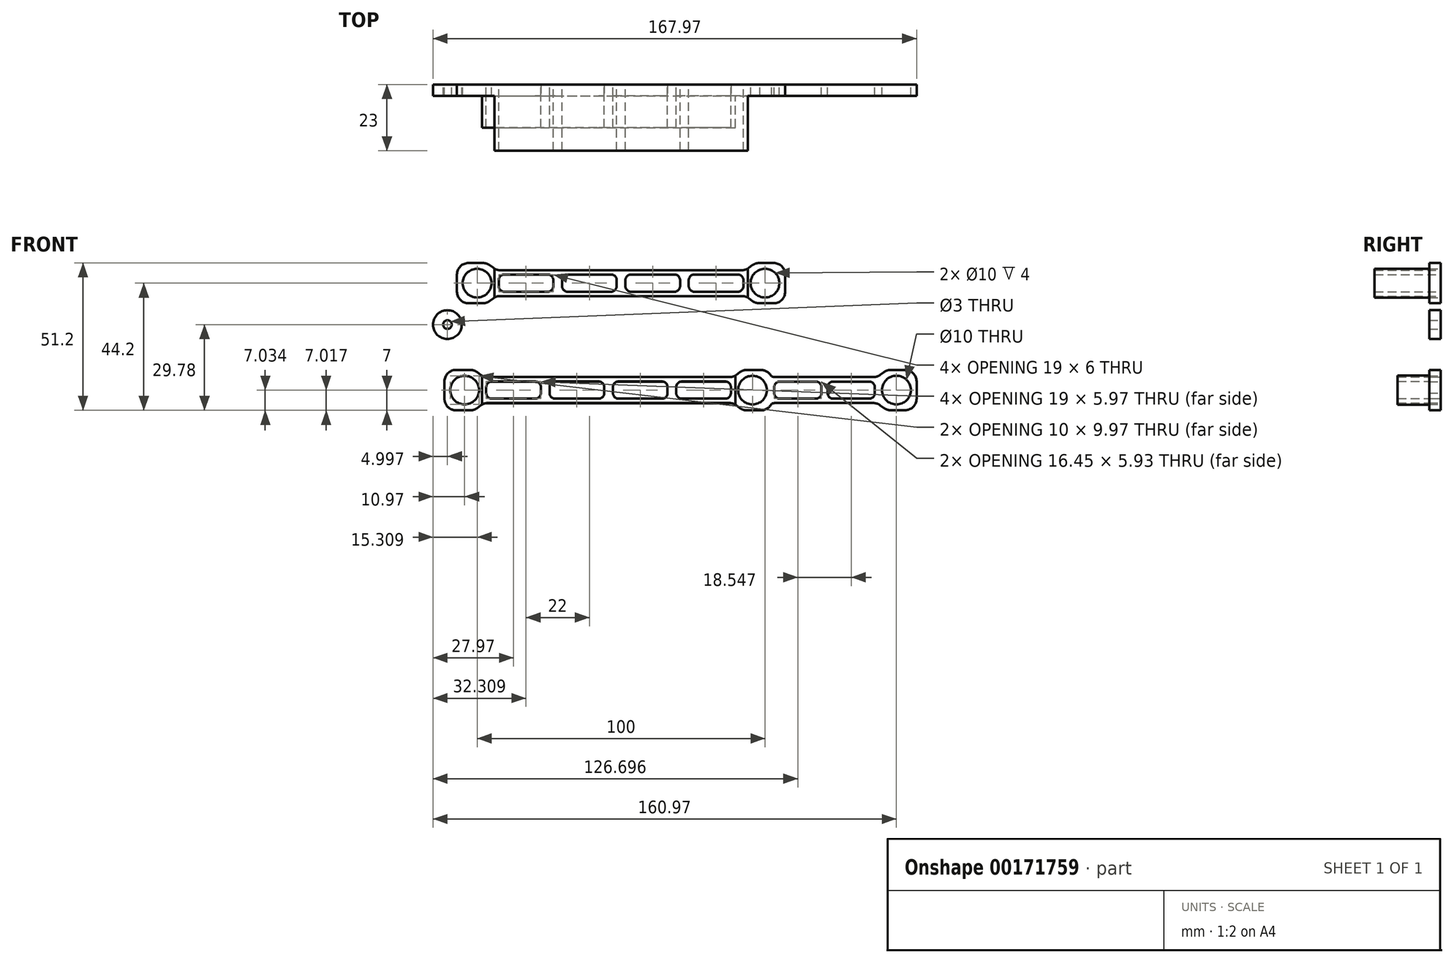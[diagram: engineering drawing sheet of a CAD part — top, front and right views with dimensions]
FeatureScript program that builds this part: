
annotation { "Feature Type Name" : "Feature", "Feature Type Description" : "" }
export const myFeature = defineFeature(function(context is Context, id is Id, definition is map)
    precondition{}
    {
        {
            var Q0;
            Q0=qCreatedBy(makeId("Front.planeOp"),FACE);
            var sketch = newSketch(context, id + "F0", { "sketchPlane" : qUnion([Q0])});
            skCircle(sketch, "E0", {"center": v(-50, 0) * mm, "radius": 5 * mm});
            skPoint(sketch, "E0.centerSnap0", {"position": v(-57, 0) * mm});
            skArc(sketch, "E1.filletArc", {"start": v(-57, -3) * mm, "mid": v(-55.83, -5.83) * mm, "end": v(-53, -7) * mm});
            skLineSegment(sketch, "E2.bottom", {"start": v(-40.5, -3) * mm, "end": v(-25.5, -3) * mm});
            skLineSegment(sketch, "E3.top", {"start": v(-18.5, -3) * mm, "end": v(-3.5, -3) * mm});
            skLineSegment(sketch, "E4", {"start": v(0, 16.94) * mm, "end": v(0, -22.86) * mm, "construction": true});
            skArc(sketch, "E5.filletArc", {"start": v(-25.5, -3) * mm, "mid": v(-24.09, -2.41) * mm, "end": v(-23.5, -1) * mm});
            skArc(sketch, "E6.filletArc", {"start": v(-42.5, -1) * mm, "mid": v(-41.91, -2.41) * mm, "end": v(-40.5, -3) * mm});
            skArc(sketch, "E7.filletArc", {"start": v(-20.5, -1) * mm, "mid": v(-19.91, -2.41) * mm, "end": v(-18.5, -3) * mm});
            skArc(sketch, "E8.filletArc", {"start": v(-3.5, -3) * mm, "mid": v(-2.09, -2.41) * mm, "end": v(-1.5, -1) * mm});
            skLineSegment(sketch, "E9", {"start": v(0, 0) * mm, "end": v(-64.75, 0) * mm, "construction": true});
            skLineSegment(sketch, "E10", {"start": v(-57, -3) * mm, "end": v(-57, 0) * mm});
            skLineSegment(sketch, "E11", {"start": v(-53, -7) * mm, "end": v(-48, -7) * mm});
            skLineSegment(sketch, "E12", {"start": v(-42, -4.5) * mm, "end": v(0, -4.5) * mm});
            skLineSegment(sketch, "E13", {"start": v(-42.5, -1) * mm, "end": v(-42.5, 0) * mm});
            skLineSegment(sketch, "E14", {"start": v(-23.5, -1) * mm, "end": v(-23.5, 0) * mm});
            skLineSegment(sketch, "E15", {"start": v(-20.5, -1) * mm, "end": v(-20.5, 0) * mm});
            skLineSegment(sketch, "E16", {"start": v(-1.5, -1) * mm, "end": v(-1.5, 0) * mm});
            skLineSegment(sketch, "E17", {"start": v(-45.6, -6.2) * mm, "end": v(-44.4, -5.3) * mm});
            skPoint(sketch, "E18.visualSharp", {"position": v(-46.67, -7) * mm});
            skArc(sketch, "E18.filletArc", {"start": v(-48, -7) * mm, "mid": v(-46.74, -6.8) * mm, "end": v(-45.6, -6.2) * mm});
            skPoint(sketch, "E19.visualSharp", {"position": v(-43.33, -4.5) * mm});
            skArc(sketch, "E19.filletArc", {"start": v(-42, -4.5) * mm, "mid": v(-43.26, -4.7) * mm, "end": v(-44.4, -5.3) * mm});
            skLineSegment(sketch, "E20.MirrorCS", {"start": v(-20.5, 1) * mm, "end": v(-20.5, 0) * mm});
            skLineSegment(sketch, "E21.MirrorCS", {"start": v(-23.5, 1) * mm, "end": v(-23.5, 0) * mm});
            skLineSegment(sketch, "E22.MirrorCS", {"start": v(-45.6, 6.2) * mm, "end": v(-44.4, 5.3) * mm});
            skLineSegment(sketch, "E23.MirrorCS", {"start": v(-42.5, 1) * mm, "end": v(-42.5, 0) * mm});
            skLineSegment(sketch, "E24.MirrorCS", {"start": v(-1.5, 1) * mm, "end": v(-1.5, 0) * mm});
            skArc(sketch, "E25.MirrorCS", {"start": v(-48, 7) * mm, "mid": v(-46.74, 6.8) * mm, "end": v(-45.6, 6.2) * mm});
            skArc(sketch, "E26.MirrorCS", {"start": v(-42, 4.5) * mm, "mid": v(-43.26, 4.7) * mm, "end": v(-44.4, 5.3) * mm});
            skLineSegment(sketch, "E27.MirrorCS", {"start": v(-40.5, 3) * mm, "end": v(-25.5, 3) * mm});
            skLineSegment(sketch, "E28.MirrorCS", {"start": v(-42, 4.5) * mm, "end": v(0, 4.5) * mm});
            skArc(sketch, "E29.MirrorCS", {"start": v(-57, 3) * mm, "mid": v(-55.83, 5.83) * mm, "end": v(-53, 7) * mm});
            skLineSegment(sketch, "E30.MirrorCS", {"start": v(-53, 7) * mm, "end": v(-48, 7) * mm});
            skLineSegment(sketch, "E31.MirrorCS", {"start": v(-57, 3) * mm, "end": v(-57, 0) * mm});
            skPoint(sketch, "E32.MirrorP", {"position": v(-46.67, 7) * mm});
            skLineSegment(sketch, "E33.MirrorCS", {"start": v(-18.5, 3) * mm, "end": v(-3.5, 3) * mm});
            skArc(sketch, "E34.MirrorCS", {"start": v(-3.5, 3) * mm, "mid": v(-2.09, 2.41) * mm, "end": v(-1.5, 1) * mm});
            skPoint(sketch, "E35.MirrorP", {"position": v(-43.33, 4.5) * mm});
            skArc(sketch, "E36.MirrorCS", {"start": v(-20.5, 1) * mm, "mid": v(-19.91, 2.41) * mm, "end": v(-18.5, 3) * mm});
            skArc(sketch, "E37.MirrorCS", {"start": v(-42.5, 1) * mm, "mid": v(-41.91, 2.41) * mm, "end": v(-40.5, 3) * mm});
            skArc(sketch, "E38.MirrorCS", {"start": v(-25.5, 3) * mm, "mid": v(-24.09, 2.41) * mm, "end": v(-23.5, 1) * mm});
            skLineSegment(sketch, "E39.MirrorCS", {"start": v(45.6, 6.2) * mm, "end": v(44.4, 5.3) * mm});
            skLineSegment(sketch, "E40.MirrorCS", {"start": v(23.5, 1) * mm, "end": v(23.5, 0) * mm});
            skLineSegment(sketch, "E41.MirrorCS", {"start": v(1.5, 1) * mm, "end": v(1.5, 0) * mm});
            skLineSegment(sketch, "E42.MirrorCS", {"start": v(42.5, -1) * mm, "end": v(42.5, 0) * mm});
            skLineSegment(sketch, "E43.MirrorCS", {"start": v(23.5, -1) * mm, "end": v(23.5, 0) * mm});
            skLineSegment(sketch, "E44.MirrorCS", {"start": v(20.5, -1) * mm, "end": v(20.5, 0) * mm});
            skLineSegment(sketch, "E45.MirrorCS", {"start": v(45.6, -6.2) * mm, "end": v(44.4, -5.3) * mm});
            skLineSegment(sketch, "E46.MirrorCS", {"start": v(20.5, 1) * mm, "end": v(20.5, 0) * mm});
            skLineSegment(sketch, "E47.MirrorCS", {"start": v(1.5, -1) * mm, "end": v(1.5, 0) * mm});
            skLineSegment(sketch, "E48.MirrorCS", {"start": v(42.5, 1) * mm, "end": v(42.5, 0) * mm});
            skArc(sketch, "E49.MirrorCS", {"start": v(48, 7) * mm, "mid": v(46.74, 6.8) * mm, "end": v(45.6, 6.2) * mm});
            skArc(sketch, "E50.MirrorCS", {"start": v(48, -7) * mm, "mid": v(46.74, -6.8) * mm, "end": v(45.6, -6.2) * mm});
            skArc(sketch, "E51.MirrorCS", {"start": v(42, -4.5) * mm, "mid": v(43.26, -4.7) * mm, "end": v(44.4, -5.3) * mm});
            skCircle(sketch, "E52.MirrorC", {"center": v(50, 0) * mm, "radius": 5 * mm});
            skPoint(sketch, "E53.MirrorP", {"position": v(57, 0) * mm});
            skArc(sketch, "E54.MirrorCS", {"start": v(42, 4.5) * mm, "mid": v(43.26, 4.7) * mm, "end": v(44.4, 5.3) * mm});
            skArc(sketch, "E55.MirrorCS", {"start": v(25.5, -3) * mm, "mid": v(24.09, -2.41) * mm, "end": v(23.5, -1) * mm});
            skLineSegment(sketch, "E56.MirrorCS", {"start": v(42, -4.5) * mm, "end": v(0, -4.5) * mm});
            skPoint(sketch, "E57.MirrorP", {"position": v(43.33, 4.5) * mm});
            skLineSegment(sketch, "E58.MirrorCS", {"start": v(18.5, -3) * mm, "end": v(3.5, -3) * mm});
            skArc(sketch, "E59.MirrorCS", {"start": v(57, -3) * mm, "mid": v(55.83, -5.83) * mm, "end": v(53, -7) * mm});
            skLineSegment(sketch, "E60.MirrorCS", {"start": v(53, -7) * mm, "end": v(48, -7) * mm});
            skArc(sketch, "E61.MirrorCS", {"start": v(25.5, 3) * mm, "mid": v(24.09, 2.41) * mm, "end": v(23.5, 1) * mm});
            skArc(sketch, "E62.MirrorCS", {"start": v(3.5, -3) * mm, "mid": v(2.09, -2.41) * mm, "end": v(1.5, -1) * mm});
            skArc(sketch, "E63.MirrorCS", {"start": v(57, 3) * mm, "mid": v(55.83, 5.83) * mm, "end": v(53, 7) * mm});
            skPoint(sketch, "E64.MirrorP", {"position": v(46.67, -7) * mm});
            skPoint(sketch, "E65.MirrorP", {"position": v(46.67, 7) * mm});
            skLineSegment(sketch, "E66.MirrorCS", {"start": v(53, 7) * mm, "end": v(48, 7) * mm});
            skPoint(sketch, "E67.MirrorP", {"position": v(43.33, -4.5) * mm});
            skArc(sketch, "E68.MirrorCS", {"start": v(42.5, 1) * mm, "mid": v(41.91, 2.41) * mm, "end": v(40.5, 3) * mm});
            skLineSegment(sketch, "E69.MirrorCS", {"start": v(42, 4.5) * mm, "end": v(0, 4.5) * mm});
            skArc(sketch, "E70.MirrorCS", {"start": v(20.5, 1) * mm, "mid": v(19.91, 2.41) * mm, "end": v(18.5, 3) * mm});
            skLineSegment(sketch, "E71.MirrorCS", {"start": v(0, 0) * mm, "end": v(64.75, 0) * mm, "construction": true});
            skArc(sketch, "E72.MirrorCS", {"start": v(3.5, 3) * mm, "mid": v(2.09, 2.41) * mm, "end": v(1.5, 1) * mm});
            skArc(sketch, "E73.MirrorCS", {"start": v(42.5, -1) * mm, "mid": v(41.91, -2.41) * mm, "end": v(40.5, -3) * mm});
            skArc(sketch, "E74.MirrorCS", {"start": v(20.5, -1) * mm, "mid": v(19.91, -2.41) * mm, "end": v(18.5, -3) * mm});
            skLineSegment(sketch, "E75.MirrorCS", {"start": v(57, 3) * mm, "end": v(57, 0) * mm});
            skLineSegment(sketch, "E76.MirrorCS", {"start": v(40.5, 3) * mm, "end": v(25.5, 3) * mm});
            skLineSegment(sketch, "E77.MirrorCS", {"start": v(40.5, -3) * mm, "end": v(25.5, -3) * mm});
            skLineSegment(sketch, "E78.MirrorCS", {"start": v(18.5, 3) * mm, "end": v(3.5, 3) * mm});
            skLineSegment(sketch, "E79.MirrorCS", {"start": v(57, -3) * mm, "end": v(57, 0) * mm});
            skSolve(sketch);
        }
        {
            var Q0;
            Q0=makeQuery(id+"F0.imprint","IMPRINT",FACE,{"disambiguationData":[TD([[makeQuery(id+"F0.imprint","IMPRINT",EDGE,{"derivedFrom":sQuery(id+"F0.wireOp",EDGE,"E1.filletArc")}),1.0]])]});
            extrude(context, id + "F1", {"entities" : qUnion([Q0]), "depth" : 4 * mm});
        }
        {
            var Q0;
            Q0=qCreatedBy(makeId("Front.planeOp"),FACE);
            var sketch = newSketch(context, id + "F2", { "sketchPlane" : qUnion([Q0])});
            skCircle(sketch, "E80", {"center": v(-55.97, 22.78) * mm, "radius": 1.5 * mm});
            skCircle(sketch, "E81", {"center": v(-55.97, 22.78) * mm, "radius": 5 * mm});
            skSolve(sketch);
        }
        {
            var Q0;
            Q0=makeQuery(id+"F2.imprint","IMPRINT",FACE,{"disambiguationData":[TD([[makeQuery(id+"F2.imprint","IMPRINT",EDGE,{"derivedFrom":sQuery(id+"F2.wireOp",EDGE,"E80")}),-1.0]])]});
            extrude(context, id + "F3", {"entities" : qUnion([Q0]), "depth" : 4 * mm});
        }
        {
            var Q0;
            Q0=qCreatedBy(makeId("Front.planeOp"),FACE);
            var sketch = newSketch(context, id + "F4", { "sketchPlane" : qUnion([Q0])});
            skCircle(sketch, "E82", {"center": v(-50, 0.03) * mm, "radius": 5 * mm});
            skPoint(sketch, "E82.centerSnap0", {"position": v(-57, 0.03) * mm});
            skArc(sketch, "E83.filletArc", {"start": v(-57, -2.97) * mm, "mid": v(-55.83, -5.8) * mm, "end": v(-53, -6.97) * mm});
            skLineSegment(sketch, "E84.bottom", {"start": v(-40.5, -2.97) * mm, "end": v(-25.5, -2.97) * mm});
            skLineSegment(sketch, "E85.top", {"start": v(-18.5, -2.97) * mm, "end": v(-3.5, -2.97) * mm});
            skLineSegment(sketch, "E86", {"start": v(0, 16.97) * mm, "end": v(0, -22.82) * mm, "construction": true});
            skArc(sketch, "E87.filletArc", {"start": v(-25.5, -2.97) * mm, "mid": v(-24.09, -2.38) * mm, "end": v(-23.5, -0.97) * mm});
            skArc(sketch, "E88.filletArc", {"start": v(-42.5, -0.97) * mm, "mid": v(-41.91, -2.38) * mm, "end": v(-40.5, -2.97) * mm});
            skArc(sketch, "E89.filletArc", {"start": v(-20.5, -0.97) * mm, "mid": v(-19.91, -2.38) * mm, "end": v(-18.5, -2.97) * mm});
            skArc(sketch, "E90.filletArc", {"start": v(-3.5, -2.97) * mm, "mid": v(-2.09, -2.38) * mm, "end": v(-1.5, -0.97) * mm});
            skLineSegment(sketch, "E91", {"start": v(0, 0.03) * mm, "end": v(-64.75, 0.03) * mm, "construction": true});
            skLineSegment(sketch, "E92", {"start": v(-57, -2.97) * mm, "end": v(-57, 0.03) * mm});
            skLineSegment(sketch, "E93", {"start": v(-53, -6.97) * mm, "end": v(-48, -6.97) * mm});
            skLineSegment(sketch, "E94", {"start": v(-42, -4.47) * mm, "end": v(0, -4.47) * mm});
            skLineSegment(sketch, "E95", {"start": v(-42.5, -0.97) * mm, "end": v(-42.5, 0.03) * mm});
            skLineSegment(sketch, "E96", {"start": v(-23.5, -0.97) * mm, "end": v(-23.5, 0.03) * mm});
            skLineSegment(sketch, "E97", {"start": v(-20.5, -0.97) * mm, "end": v(-20.5, 0.03) * mm});
            skLineSegment(sketch, "E98", {"start": v(-1.5, -0.97) * mm, "end": v(-1.5, 0.03) * mm});
            skLineSegment(sketch, "E99", {"start": v(-45.6, -6.17) * mm, "end": v(-44.4, -5.27) * mm});
            skPoint(sketch, "E100.visualSharp", {"position": v(-46.67, -6.97) * mm});
            skArc(sketch, "E100.filletArc", {"start": v(-48, -6.97) * mm, "mid": v(-46.74, -6.76) * mm, "end": v(-45.6, -6.17) * mm});
            skPoint(sketch, "E101.visualSharp", {"position": v(-43.33, -4.47) * mm});
            skArc(sketch, "E101.filletArc", {"start": v(-42, -4.47) * mm, "mid": v(-43.26, -4.67) * mm, "end": v(-44.4, -5.27) * mm});
            skLineSegment(sketch, "E102.MirrorCS", {"start": v(-20.5, 1.03) * mm, "end": v(-20.5, 0.03) * mm});
            skLineSegment(sketch, "E103.MirrorCS", {"start": v(-23.5, 1.03) * mm, "end": v(-23.5, 0.03) * mm});
            skLineSegment(sketch, "E104.MirrorCS", {"start": v(-45.6, 6.23) * mm, "end": v(-44.4, 5.33) * mm});
            skLineSegment(sketch, "E105.MirrorCS", {"start": v(-42.5, 1.03) * mm, "end": v(-42.5, 0.03) * mm});
            skLineSegment(sketch, "E106.MirrorCS", {"start": v(-1.5, 1.03) * mm, "end": v(-1.5, 0.03) * mm});
            skArc(sketch, "E107.MirrorCS", {"start": v(-48, 7.03) * mm, "mid": v(-46.74, 6.83) * mm, "end": v(-45.6, 6.23) * mm});
            skArc(sketch, "E108.MirrorCS", {"start": v(-42, 4.53) * mm, "mid": v(-43.26, 4.74) * mm, "end": v(-44.4, 5.33) * mm});
            skLineSegment(sketch, "E109.MirrorCS", {"start": v(-40.5, 3.03) * mm, "end": v(-25.5, 3.03) * mm});
            skLineSegment(sketch, "E110.MirrorCS", {"start": v(-42, 4.53) * mm, "end": v(0, 4.53) * mm});
            skArc(sketch, "E111.MirrorCS", {"start": v(-57, 3.03) * mm, "mid": v(-55.83, 5.86) * mm, "end": v(-53, 7.03) * mm});
            skLineSegment(sketch, "E112.MirrorCS", {"start": v(-53, 7.03) * mm, "end": v(-48, 7.03) * mm});
            skLineSegment(sketch, "E113.MirrorCS", {"start": v(-57, 3.03) * mm, "end": v(-57, 0.03) * mm});
            skPoint(sketch, "E114.MirrorP", {"position": v(-46.67, 7.03) * mm});
            skLineSegment(sketch, "E115.MirrorCS", {"start": v(-18.5, 3.03) * mm, "end": v(-3.5, 3.03) * mm});
            skArc(sketch, "E116.MirrorCS", {"start": v(-3.5, 3.03) * mm, "mid": v(-2.09, 2.45) * mm, "end": v(-1.5, 1.03) * mm});
            skPoint(sketch, "E117.MirrorP", {"position": v(-43.33, 4.53) * mm});
            skArc(sketch, "E118.MirrorCS", {"start": v(-20.5, 1.03) * mm, "mid": v(-19.91, 2.45) * mm, "end": v(-18.5, 3.03) * mm});
            skArc(sketch, "E119.MirrorCS", {"start": v(-42.5, 1.03) * mm, "mid": v(-41.91, 2.45) * mm, "end": v(-40.5, 3.03) * mm});
            skArc(sketch, "E120.MirrorCS", {"start": v(-25.5, 3.03) * mm, "mid": v(-24.09, 2.45) * mm, "end": v(-23.5, 1.03) * mm});
            skLineSegment(sketch, "E121.MirrorCS", {"start": v(45.6, 6.23) * mm, "end": v(44.4, 5.33) * mm});
            skLineSegment(sketch, "E122.MirrorCS", {"start": v(23.5, 1.03) * mm, "end": v(23.5, 0.03) * mm});
            skLineSegment(sketch, "E123.MirrorCS", {"start": v(1.5, 1.03) * mm, "end": v(1.5, 0.03) * mm});
            skLineSegment(sketch, "E124.MirrorCS", {"start": v(42.5, -0.97) * mm, "end": v(42.5, 0.03) * mm});
            skLineSegment(sketch, "E125.MirrorCS", {"start": v(23.5, -0.97) * mm, "end": v(23.5, 0.03) * mm});
            skLineSegment(sketch, "E126.MirrorCS", {"start": v(20.5, -0.97) * mm, "end": v(20.5, 0.03) * mm});
            skLineSegment(sketch, "E127.MirrorCS", {"start": v(45.6, -6.17) * mm, "end": v(44.4, -5.27) * mm});
            skLineSegment(sketch, "E128.MirrorCS", {"start": v(20.5, 1.03) * mm, "end": v(20.5, 0.03) * mm});
            skLineSegment(sketch, "E129.MirrorCS", {"start": v(1.5, -0.97) * mm, "end": v(1.5, 0.03) * mm});
            skLineSegment(sketch, "E130.MirrorCS", {"start": v(42.5, 1.03) * mm, "end": v(42.5, 0.03) * mm});
            skArc(sketch, "E131.MirrorCS", {"start": v(48, 7.03) * mm, "mid": v(46.74, 6.83) * mm, "end": v(45.6, 6.23) * mm});
            skArc(sketch, "E132.MirrorCS", {"start": v(48, -6.97) * mm, "mid": v(46.74, -6.76) * mm, "end": v(45.6, -6.17) * mm});
            skArc(sketch, "E133.MirrorCS", {"start": v(42, -4.47) * mm, "mid": v(43.26, -4.67) * mm, "end": v(44.4, -5.27) * mm});
            skCircle(sketch, "E134.MirrorC", {"center": v(50, 0.03) * mm, "radius": 5 * mm});
            skArc(sketch, "E135.MirrorCS", {"start": v(42, 4.53) * mm, "mid": v(43.26, 4.74) * mm, "end": v(44.4, 5.33) * mm});
            skArc(sketch, "E136.MirrorCS", {"start": v(25.5, -2.97) * mm, "mid": v(24.09, -2.38) * mm, "end": v(23.5, -0.97) * mm});
            skLineSegment(sketch, "E137.MirrorCS", {"start": v(42, -4.47) * mm, "end": v(0, -4.47) * mm});
            skPoint(sketch, "E138.MirrorP", {"position": v(43.33, 4.53) * mm});
            skLineSegment(sketch, "E139.MirrorCS", {"start": v(18.5, -2.97) * mm, "end": v(3.5, -2.97) * mm});
            skArc(sketch, "E140.MirrorCS", {"start": v(25.5, 3.03) * mm, "mid": v(24.09, 2.45) * mm, "end": v(23.5, 1.03) * mm});
            skArc(sketch, "E141.MirrorCS", {"start": v(3.5, -2.97) * mm, "mid": v(2.09, -2.38) * mm, "end": v(1.5, -0.97) * mm});
            skPoint(sketch, "E142.MirrorP", {"position": v(46.67, -6.97) * mm});
            skPoint(sketch, "E143.MirrorP", {"position": v(46.67, 7.03) * mm});
            skPoint(sketch, "E144.MirrorP", {"position": v(43.33, -4.47) * mm});
            skArc(sketch, "E145.MirrorCS", {"start": v(42.5, 1.03) * mm, "mid": v(41.91, 2.45) * mm, "end": v(40.5, 3.03) * mm});
            skLineSegment(sketch, "E146.MirrorCS", {"start": v(42, 4.53) * mm, "end": v(0, 4.53) * mm});
            skArc(sketch, "E147.MirrorCS", {"start": v(20.5, 1.03) * mm, "mid": v(19.91, 2.45) * mm, "end": v(18.5, 3.03) * mm});
            skLineSegment(sketch, "E148.MirrorCS", {"start": v(0, 0.03) * mm, "end": v(64.75, 0.03) * mm, "construction": true});
            skArc(sketch, "E149.MirrorCS", {"start": v(3.5, 3.03) * mm, "mid": v(2.09, 2.45) * mm, "end": v(1.5, 1.03) * mm});
            skArc(sketch, "E150.MirrorCS", {"start": v(42.5, -0.97) * mm, "mid": v(41.91, -2.38) * mm, "end": v(40.5, -2.97) * mm});
            skArc(sketch, "E151.MirrorCS", {"start": v(20.5, -0.97) * mm, "mid": v(19.91, -2.38) * mm, "end": v(18.5, -2.97) * mm});
            skLineSegment(sketch, "E152.MirrorCS", {"start": v(40.5, 3.03) * mm, "end": v(25.5, 3.03) * mm});
            skLineSegment(sketch, "E153.MirrorCS", {"start": v(40.5, -2.97) * mm, "end": v(25.5, -2.97) * mm});
            skLineSegment(sketch, "E154.MirrorCS", {"start": v(18.5, 3.03) * mm, "end": v(3.5, 3.03) * mm});
            skLineSegment(sketch, "E155", {"start": v(25, -18.9) * mm, "end": v(25, 17.57) * mm, "construction": true});
            skLineSegment(sketch, "E156.MirrorCS", {"start": v(95.6, 6.23) * mm, "end": v(94.4, 5.33) * mm});
            skLineSegment(sketch, "E157.MirrorCS", {"start": v(95.6, -6.17) * mm, "end": v(94.4, -5.27) * mm});
            skCircle(sketch, "E158.MirrorC", {"center": v(100, 0.03) * mm, "radius": 5 * mm});
            skPoint(sketch, "E159.MirrorP", {"position": v(107, 0.03) * mm});
            skArc(sketch, "E160.MirrorCS", {"start": v(98, 7.03) * mm, "mid": v(96.74, 6.83) * mm, "end": v(95.6, 6.23) * mm});
            skArc(sketch, "E161.MirrorCS", {"start": v(98, -6.97) * mm, "mid": v(96.74, -6.76) * mm, "end": v(95.6, -6.17) * mm});
            skLineSegment(sketch, "E162.MirrorCS", {"start": v(107, 3.03) * mm, "end": v(107, 0.03) * mm});
            skPoint(sketch, "E163.MirrorP", {"position": v(96.67, -6.97) * mm});
            skLineSegment(sketch, "E164.MirrorCS", {"start": v(103, 7.03) * mm, "end": v(98, 7.03) * mm});
            skLineSegment(sketch, "E165.MirrorCS", {"start": v(103, -6.97) * mm, "end": v(98, -6.97) * mm});
            skLineSegment(sketch, "E166.MirrorCS", {"start": v(107, -2.97) * mm, "end": v(107, 0.03) * mm});
            skArc(sketch, "E167.MirrorCS", {"start": v(107, -2.97) * mm, "mid": v(105.83, -5.8) * mm, "end": v(103, -6.97) * mm});
            skArc(sketch, "E168.MirrorCS", {"start": v(107, 3.03) * mm, "mid": v(105.83, 5.86) * mm, "end": v(103, 7.03) * mm});
            skPoint(sketch, "E169.MirrorP", {"position": v(96.67, 7.03) * mm});
            skPoint(sketch, "E170.MirrorP", {"position": v(93.33, -4.47) * mm});
            skPoint(sketch, "E171.MirrorP", {"position": v(93.33, 4.53) * mm});
            skArc(sketch, "E172.MirrorCS", {"start": v(92, 4.53) * mm, "mid": v(93.26, 4.74) * mm, "end": v(94.4, 5.33) * mm});
            skArc(sketch, "E173.MirrorCS", {"start": v(92, -4.47) * mm, "mid": v(93.26, -4.67) * mm, "end": v(94.4, -5.27) * mm});
            skLineSegment(sketch, "E174", {"start": v(50, -9.2) * mm, "end": v(50, 12.58) * mm, "construction": true});
            skLineSegment(sketch, "E175", {"start": v(48, 7.03) * mm, "end": v(50, 7.03) * mm});
            skLineSegment(sketch, "E176", {"start": v(48, -6.97) * mm, "end": v(50, -6.97) * mm});
            skLineSegment(sketch, "E177.MirrorCS", {"start": v(52, 7.03) * mm, "end": v(50, 7.03) * mm});
            skArc(sketch, "E178.MirrorCS", {"start": v(52, 7.03) * mm, "mid": v(53.26, 6.83) * mm, "end": v(54.4, 6.23) * mm});
            skLineSegment(sketch, "E179.MirrorCS", {"start": v(54.4, 6.23) * mm, "end": v(55.6, 5.33) * mm});
            skArc(sketch, "E180.MirrorCS", {"start": v(58, 4.53) * mm, "mid": v(56.74, 4.74) * mm, "end": v(55.6, 5.33) * mm});
            skArc(sketch, "E181.MirrorCS", {"start": v(58, -4.47) * mm, "mid": v(56.74, -4.67) * mm, "end": v(55.6, -5.27) * mm});
            skLineSegment(sketch, "E182.MirrorCS", {"start": v(54.4, -6.17) * mm, "end": v(55.6, -5.27) * mm});
            skArc(sketch, "E183.MirrorCS", {"start": v(52, -6.97) * mm, "mid": v(53.26, -6.76) * mm, "end": v(54.4, -6.17) * mm});
            skLineSegment(sketch, "E184.MirrorCS", {"start": v(52, -6.97) * mm, "end": v(50, -6.97) * mm});
            skLineSegment(sketch, "E185", {"start": v(58, 4.53) * mm, "end": v(92, 4.53) * mm});
            skLineSegment(sketch, "E186", {"start": v(58, -4.47) * mm, "end": v(92, -4.47) * mm});
            skLineSegment(sketch, "E187.bottom", {"start": v(71.95, -2.97) * mm, "end": v(59.5, -2.97) * mm});
            skLineSegment(sketch, "E187.top", {"start": v(71.95, 2.97) * mm, "end": v(59.5, 2.97) * mm});
            skLineSegment(sketch, "E187.left", {"start": v(73.95, -0.97) * mm, "end": v(73.95, 0.97) * mm});
            skLineSegment(sketch, "E187.right", {"start": v(57.5, -0.97) * mm, "end": v(57.5, 0.97) * mm});
            skPoint(sketch, "E187.middle", {"position": v(65.73, 0) * mm});
            skPoint(sketch, "E188.visualSharp", {"position": v(57.5, 2.97) * mm});
            skArc(sketch, "E188.filletArc", {"start": v(59.5, 2.97) * mm, "mid": v(58.09, 2.38) * mm, "end": v(57.5, 0.97) * mm});
            skPoint(sketch, "E189.visualSharp", {"position": v(57.5, -2.97) * mm});
            skArc(sketch, "E189.filletArc", {"start": v(57.5, -0.97) * mm, "mid": v(58.09, -2.38) * mm, "end": v(59.5, -2.97) * mm});
            skPoint(sketch, "E190.visualSharp", {"position": v(73.95, -2.97) * mm});
            skArc(sketch, "E190.filletArc", {"start": v(71.95, -2.97) * mm, "mid": v(73.37, -2.38) * mm, "end": v(73.95, -0.97) * mm});
            skPoint(sketch, "E191.visualSharp", {"position": v(73.95, 2.97) * mm});
            skArc(sketch, "E191.filletArc", {"start": v(73.95, 0.97) * mm, "mid": v(73.37, 2.38) * mm, "end": v(71.95, 2.97) * mm});
            skLineSegment(sketch, "E192", {"start": v(75, -8.26) * mm, "end": v(75, 11.45) * mm, "construction": true});
            skPoint(sketch, "E192.startSnap0", {"position": v(75, -4.47) * mm});
            skArc(sketch, "E193.MirrorCS", {"start": v(90.5, 2.97) * mm, "mid": v(91.91, 2.38) * mm, "end": v(92.5, 0.97) * mm});
            skLineSegment(sketch, "E194.MirrorCS", {"start": v(150, 0.03) * mm, "end": v(85.25, 0.03) * mm, "construction": true});
            skLineSegment(sketch, "E195.MirrorCS", {"start": v(92.5, -0.97) * mm, "end": v(92.5, 0.97) * mm});
            skPoint(sketch, "E196.MirrorP", {"position": v(76.05, 2.97) * mm});
            skArc(sketch, "E197.MirrorCS", {"start": v(76.05, 0.97) * mm, "mid": v(76.63, 2.38) * mm, "end": v(78.05, 2.97) * mm});
            skArc(sketch, "E198.MirrorCS", {"start": v(78.05, -2.97) * mm, "mid": v(76.63, -2.38) * mm, "end": v(76.05, -0.97) * mm});
            skPoint(sketch, "E199.MirrorP", {"position": v(76.05, -2.97) * mm});
            skPoint(sketch, "E200.MirrorP", {"position": v(92.5, -2.97) * mm});
            skLineSegment(sketch, "E201.MirrorCS", {"start": v(76.05, -0.97) * mm, "end": v(76.05, 0.97) * mm});
            skPoint(sketch, "E202.MirrorP", {"position": v(92.5, 2.97) * mm});
            skPoint(sketch, "E203.MirrorP", {"position": v(84.27, 0) * mm});
            skLineSegment(sketch, "E204.MirrorCS", {"start": v(78.05, 2.97) * mm, "end": v(90.5, 2.97) * mm});
            skLineSegment(sketch, "E205.MirrorCS", {"start": v(78.05, -2.97) * mm, "end": v(90.5, -2.97) * mm});
            skArc(sketch, "E206.MirrorCS", {"start": v(92.5, -0.97) * mm, "mid": v(91.91, -2.38) * mm, "end": v(90.5, -2.97) * mm});
            skLineSegment(sketch, "E207", {"start": v(-44, 5.07) * mm, "end": v(-44, -5) * mm});
            skLineSegment(sketch, "E208", {"start": v(44, 5.07) * mm, "end": v(44, -5) * mm});
            skSolve(sketch);
        }
        {
            var Q0;
            Q0=makeQuery(id+"F4.imprint","IMPRINT",FACE,{"disambiguationData":[TD([[makeQuery(id+"F4.imprint","IMPRINT",EDGE,{"derivedFrom":sQuery(id+"F4.wireOp",EDGE,"E83.filletArc")}),1.0]])]});
            var Q1;
            {var subQ5=sQuery(id+"F4.wireOp",EDGE,"E84.bottom");Q1=makeQuery(id+"F4.imprint","IMPRINT",FACE,{"disambiguationData":[TD([[makeQuery(id+"F4.imprint","IMPRINT",EDGE,{"derivedFrom":subQ5}),-1.0]])]});}
            var Q2;
            Q2=makeQuery(id+"F4.imprint","IMPRINT",FACE,{"disambiguationData":[TD([[makeQuery(id+"F4.imprint","IMPRINT",EDGE,{"derivedFrom":sQuery(id+"F4.wireOp",EDGE,"E121.MirrorCS")}),1.0]])]});
            extrude(context, id + "F5", {"entities" : qUnion([Q0, Q1, Q2]), "depth" : 4 * mm});
        }
        {
            var Q0;
            {var subQ5=sQuery(id+"F4.wireOp",EDGE,"E84.bottom");Q0=makeQuery(id+"F4.imprint","IMPRINT",FACE,{"disambiguationData":[TD([[makeQuery(id+"F4.imprint","IMPRINT",EDGE,{"derivedFrom":subQ5}),-1.0]])]});}
            extrude(context, id + "F6", {"entities" : qUnion([Q0]), "operationType" : NewBodyOperationType.ADD, "depth" : 15 * mm});
        }
        {
            var Q0;
            Q0=qCreatedBy(makeId("Front.planeOp"),FACE);
            var sketch = newSketch(context, id + "F7", { "sketchPlane" : qUnion([Q0])});
            skCircle(sketch, "E209", {"center": v(-45.66, 37.2) * mm, "radius": 5 * mm});
            skPoint(sketch, "E209.centerSnap0", {"position": v(-52.66, 37.2) * mm});
            skArc(sketch, "E210.filletArc", {"start": v(-52.66, 34.2) * mm, "mid": v(-51.49, 31.37) * mm, "end": v(-48.66, 30.2) * mm});
            skLineSegment(sketch, "E211.bottom", {"start": v(-36.16, 34.2) * mm, "end": v(-21.16, 34.2) * mm});
            skLineSegment(sketch, "E212.top", {"start": v(-14.16, 34.2) * mm, "end": v(0.84, 34.2) * mm});
            skLineSegment(sketch, "E213", {"start": v(4.34, 51.7) * mm, "end": v(4.34, 22.7) * mm, "construction": true});
            skArc(sketch, "E214.filletArc", {"start": v(-21.16, 34.2) * mm, "mid": v(-19.75, 34.79) * mm, "end": v(-19.16, 36.2) * mm});
            skArc(sketch, "E215.filletArc", {"start": v(-38.16, 36.2) * mm, "mid": v(-37.57, 34.79) * mm, "end": v(-36.16, 34.2) * mm});
            skArc(sketch, "E216.filletArc", {"start": v(-16.16, 36.2) * mm, "mid": v(-15.57, 34.79) * mm, "end": v(-14.16, 34.2) * mm});
            skArc(sketch, "E217.filletArc", {"start": v(0.84, 34.2) * mm, "mid": v(2.25, 34.79) * mm, "end": v(2.84, 36.2) * mm});
            skLineSegment(sketch, "E218", {"start": v(4.34, 37.2) * mm, "end": v(-62.66, 37.2) * mm, "construction": true});
            skLineSegment(sketch, "E219", {"start": v(-52.66, 34.2) * mm, "end": v(-52.66, 37.2) * mm});
            skLineSegment(sketch, "E220", {"start": v(-48.66, 30.2) * mm, "end": v(-43.66, 30.2) * mm});
            skLineSegment(sketch, "E221", {"start": v(-37.66, 32.7) * mm, "end": v(4.34, 32.7) * mm});
            skLineSegment(sketch, "E222", {"start": v(-38.16, 36.2) * mm, "end": v(-38.16, 37.2) * mm});
            skLineSegment(sketch, "E223", {"start": v(-19.16, 36.2) * mm, "end": v(-19.16, 37.2) * mm});
            skLineSegment(sketch, "E224", {"start": v(-16.16, 36.2) * mm, "end": v(-16.16, 37.2) * mm});
            skLineSegment(sketch, "E225", {"start": v(2.84, 36.2) * mm, "end": v(2.84, 37.2) * mm});
            skLineSegment(sketch, "E226", {"start": v(-41.26, 31) * mm, "end": v(-40.06, 31.9) * mm});
            skPoint(sketch, "E227.visualSharp", {"position": v(-42.33, 30.2) * mm});
            skArc(sketch, "E227.filletArc", {"start": v(-43.66, 30.2) * mm, "mid": v(-42.4, 30.4) * mm, "end": v(-41.26, 31) * mm});
            skPoint(sketch, "E228.visualSharp", {"position": v(-39, 32.7) * mm});
            skArc(sketch, "E228.filletArc", {"start": v(-37.66, 32.7) * mm, "mid": v(-38.93, 32.5) * mm, "end": v(-40.06, 31.9) * mm});
            skLineSegment(sketch, "E229.MirrorCS", {"start": v(-16.16, 38.2) * mm, "end": v(-16.16, 37.2) * mm});
            skLineSegment(sketch, "E230.MirrorCS", {"start": v(-19.16, 38.2) * mm, "end": v(-19.16, 37.2) * mm});
            skLineSegment(sketch, "E231.MirrorCS", {"start": v(-41.26, 43.4) * mm, "end": v(-40.06, 42.5) * mm});
            skLineSegment(sketch, "E232.MirrorCS", {"start": v(-38.16, 38.2) * mm, "end": v(-38.16, 37.2) * mm});
            skLineSegment(sketch, "E233.MirrorCS", {"start": v(2.84, 38.2) * mm, "end": v(2.84, 37.2) * mm});
            skArc(sketch, "E234.MirrorCS", {"start": v(-43.66, 44.2) * mm, "mid": v(-42.4, 44) * mm, "end": v(-41.26, 43.4) * mm});
            skArc(sketch, "E235.MirrorCS", {"start": v(-37.66, 41.7) * mm, "mid": v(-38.93, 41.9) * mm, "end": v(-40.06, 42.5) * mm});
            skLineSegment(sketch, "E236.MirrorCS", {"start": v(-36.16, 40.2) * mm, "end": v(-21.16, 40.2) * mm});
            skLineSegment(sketch, "E237.MirrorCS", {"start": v(-37.66, 41.7) * mm, "end": v(4.34, 41.7) * mm});
            skArc(sketch, "E238.MirrorCS", {"start": v(-52.66, 40.2) * mm, "mid": v(-51.49, 43.03) * mm, "end": v(-48.66, 44.2) * mm});
            skLineSegment(sketch, "E239.MirrorCS", {"start": v(-48.66, 44.2) * mm, "end": v(-43.66, 44.2) * mm});
            skLineSegment(sketch, "E240.MirrorCS", {"start": v(-52.66, 40.2) * mm, "end": v(-52.66, 37.2) * mm});
            skPoint(sketch, "E241.MirrorP", {"position": v(-42.33, 44.2) * mm});
            skLineSegment(sketch, "E242.MirrorCS", {"start": v(-14.16, 40.2) * mm, "end": v(0.84, 40.2) * mm});
            skArc(sketch, "E243.MirrorCS", {"start": v(0.84, 40.2) * mm, "mid": v(2.25, 39.61) * mm, "end": v(2.84, 38.2) * mm});
            skPoint(sketch, "E244.MirrorP", {"position": v(-39, 41.7) * mm});
            skArc(sketch, "E245.MirrorCS", {"start": v(-16.16, 38.2) * mm, "mid": v(-15.57, 39.61) * mm, "end": v(-14.16, 40.2) * mm});
            skArc(sketch, "E246.MirrorCS", {"start": v(-38.16, 38.2) * mm, "mid": v(-37.57, 39.61) * mm, "end": v(-36.16, 40.2) * mm});
            skArc(sketch, "E247.MirrorCS", {"start": v(-21.16, 40.2) * mm, "mid": v(-19.75, 39.61) * mm, "end": v(-19.16, 38.2) * mm});
            skLineSegment(sketch, "E248.MirrorCS", {"start": v(49.94, 43.4) * mm, "end": v(48.74, 42.5) * mm});
            skLineSegment(sketch, "E249.MirrorCS", {"start": v(27.84, 38.2) * mm, "end": v(27.84, 37.2) * mm});
            skLineSegment(sketch, "E250.MirrorCS", {"start": v(5.84, 38.2) * mm, "end": v(5.84, 37.2) * mm});
            skLineSegment(sketch, "E251.MirrorCS", {"start": v(46.84, 36.2) * mm, "end": v(46.84, 37.2) * mm});
            skLineSegment(sketch, "E252.MirrorCS", {"start": v(27.84, 36.2) * mm, "end": v(27.84, 37.2) * mm});
            skLineSegment(sketch, "E253.MirrorCS", {"start": v(24.84, 36.2) * mm, "end": v(24.84, 37.2) * mm});
            skLineSegment(sketch, "E254.MirrorCS", {"start": v(49.94, 31) * mm, "end": v(48.74, 31.9) * mm});
            skLineSegment(sketch, "E255.MirrorCS", {"start": v(24.84, 38.2) * mm, "end": v(24.84, 37.2) * mm});
            skLineSegment(sketch, "E256.MirrorCS", {"start": v(5.84, 36.2) * mm, "end": v(5.84, 37.2) * mm});
            skLineSegment(sketch, "E257.MirrorCS", {"start": v(46.84, 38.2) * mm, "end": v(46.84, 37.2) * mm});
            skArc(sketch, "E258.MirrorCS", {"start": v(52.34, 44.2) * mm, "mid": v(51.07, 44) * mm, "end": v(49.94, 43.4) * mm});
            skArc(sketch, "E259.MirrorCS", {"start": v(52.34, 30.2) * mm, "mid": v(51.07, 30.4) * mm, "end": v(49.94, 31) * mm});
            skArc(sketch, "E260.MirrorCS", {"start": v(46.34, 32.7) * mm, "mid": v(47.6, 32.5) * mm, "end": v(48.74, 31.9) * mm});
            skCircle(sketch, "E261.MirrorC", {"center": v(54.34, 37.2) * mm, "radius": 5 * mm});
            skPoint(sketch, "E262.MirrorP", {"position": v(61.34, 37.2) * mm});
            skArc(sketch, "E263.MirrorCS", {"start": v(46.34, 41.7) * mm, "mid": v(47.6, 41.9) * mm, "end": v(48.74, 42.5) * mm});
            skArc(sketch, "E264.MirrorCS", {"start": v(29.84, 34.2) * mm, "mid": v(28.43, 34.79) * mm, "end": v(27.84, 36.2) * mm});
            skLineSegment(sketch, "E265.MirrorCS", {"start": v(46.34, 32.7) * mm, "end": v(4.34, 32.7) * mm});
            skPoint(sketch, "E266.MirrorP", {"position": v(47.67, 41.7) * mm});
            skLineSegment(sketch, "E267.MirrorCS", {"start": v(22.84, 34.2) * mm, "end": v(7.84, 34.2) * mm});
            skArc(sketch, "E268.MirrorCS", {"start": v(61.34, 34.2) * mm, "mid": v(60.17, 31.37) * mm, "end": v(57.34, 30.2) * mm});
            skLineSegment(sketch, "E269.MirrorCS", {"start": v(57.34, 30.2) * mm, "end": v(52.34, 30.2) * mm});
            skArc(sketch, "E270.MirrorCS", {"start": v(29.84, 40.2) * mm, "mid": v(28.43, 39.61) * mm, "end": v(27.84, 38.2) * mm});
            skArc(sketch, "E271.MirrorCS", {"start": v(7.84, 34.2) * mm, "mid": v(6.43, 34.79) * mm, "end": v(5.84, 36.2) * mm});
            skArc(sketch, "E272.MirrorCS", {"start": v(61.34, 40.2) * mm, "mid": v(60.17, 43.03) * mm, "end": v(57.34, 44.2) * mm});
            skPoint(sketch, "E273.MirrorP", {"position": v(51, 30.2) * mm});
            skPoint(sketch, "E274.MirrorP", {"position": v(51, 44.2) * mm});
            skLineSegment(sketch, "E275.MirrorCS", {"start": v(57.34, 44.2) * mm, "end": v(52.34, 44.2) * mm});
            skPoint(sketch, "E276.MirrorP", {"position": v(47.67, 32.7) * mm});
            skArc(sketch, "E277.MirrorCS", {"start": v(46.84, 38.2) * mm, "mid": v(46.25, 39.61) * mm, "end": v(44.84, 40.2) * mm});
            skLineSegment(sketch, "E278.MirrorCS", {"start": v(46.34, 41.7) * mm, "end": v(4.34, 41.7) * mm});
            skArc(sketch, "E279.MirrorCS", {"start": v(24.84, 38.2) * mm, "mid": v(24.25, 39.61) * mm, "end": v(22.84, 40.2) * mm});
            skLineSegment(sketch, "E280.MirrorCS", {"start": v(4.34, 37.2) * mm, "end": v(71.34, 37.2) * mm, "construction": true});
            skArc(sketch, "E281.MirrorCS", {"start": v(7.84, 40.2) * mm, "mid": v(6.43, 39.61) * mm, "end": v(5.84, 38.2) * mm});
            skArc(sketch, "E282.MirrorCS", {"start": v(46.84, 36.2) * mm, "mid": v(46.25, 34.79) * mm, "end": v(44.84, 34.2) * mm});
            skArc(sketch, "E283.MirrorCS", {"start": v(24.84, 36.2) * mm, "mid": v(24.25, 34.79) * mm, "end": v(22.84, 34.2) * mm});
            skLineSegment(sketch, "E284.MirrorCS", {"start": v(61.34, 40.2) * mm, "end": v(61.34, 37.2) * mm});
            skLineSegment(sketch, "E285.MirrorCS", {"start": v(44.84, 40.2) * mm, "end": v(29.84, 40.2) * mm});
            skLineSegment(sketch, "E286.MirrorCS", {"start": v(44.84, 34.2) * mm, "end": v(29.84, 34.2) * mm});
            skLineSegment(sketch, "E287.MirrorCS", {"start": v(22.84, 40.2) * mm, "end": v(7.84, 40.2) * mm});
            skLineSegment(sketch, "E288.MirrorCS", {"start": v(61.34, 34.2) * mm, "end": v(61.34, 37.2) * mm});
            skLineSegment(sketch, "E289", {"start": v(-39.66, 32.16) * mm, "end": v(-39.66, 42.24) * mm});
            skLineSegment(sketch, "E290", {"start": v(48.34, 42.24) * mm, "end": v(48.34, 32.16) * mm});
            skSolve(sketch);
        }
        {
            var Q0;
            Q0=makeQuery(id+"F7.imprint","IMPRINT",FACE,{"disambiguationData":[TD([[makeQuery(id+"F7.imprint","IMPRINT",EDGE,{"derivedFrom":sQuery(id+"F7.wireOp",EDGE,"E210.filletArc")}),1.0]])]});
            var Q1;
            {var subQ4=sQuery(id+"F7.wireOp",EDGE,"E248.MirrorCS");Q1=makeQuery(id+"F7.imprint","IMPRINT",FACE,{"disambiguationData":[TD([[makeQuery(id+"F7.imprint","IMPRINT",EDGE,{"derivedFrom":subQ4}),1.0]])]});}
            var Q2;
            Q2=makeQuery(id+"F7.imprint","IMPRINT",FACE,{"disambiguationData":[TD([[makeQuery(id+"F7.imprint","IMPRINT",EDGE,{"derivedFrom":sQuery(id+"F7.wireOp",EDGE,"E211.bottom")}),-1.0]])]});
            extrude(context, id + "F8", {"entities" : qUnion([Q0, Q1, Q2]), "depth" : 4 * mm});
        }
        {
            var Q0;
            Q0=makeQuery(id+"F7.imprint","IMPRINT",FACE,{"disambiguationData":[TD([[makeQuery(id+"F7.imprint","IMPRINT",EDGE,{"derivedFrom":sQuery(id+"F7.wireOp",EDGE,"E211.bottom")}),-1.0]])]});
            extrude(context, id + "F9", {"entities" : qUnion([Q0]), "operationType" : NewBodyOperationType.ADD, "depth" : 23 * mm});
        }
    });
